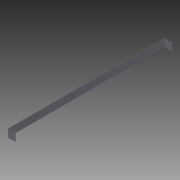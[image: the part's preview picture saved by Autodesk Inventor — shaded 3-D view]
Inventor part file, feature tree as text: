
AUTODESK INVENTOR PART (.ipt)
format: ipt  version: 2013 (Build 170138000, 138)  size: 81,920 bytes
history: native  units: in
note: dims shown in document units (in); Inventor stores cm internally (conversion verified against a paired STEP export)
features: extrude x2, sketch x2
ambient origin geometry x8: Origin, YZ Plane, XZ Plane, XY Plane, X Axis, Y Axis, Z Axis, Center Point
bodies: Solid1 (feature_tree)
feature tree (4):
  extrude  "Extrusion1"  Depth=20.5in
  extrude  "Extrusion2"  Depth=0.01in
  sketch  "Sketch1"  dims[d0=1.0in d1=20.5in]
  sketch  "Sketch2"  dims[d2=0.01in d3=0.0in d4=0.01in d5=1.0in d6=0.01in d7=1.0in d8=1.0in d9=0.0in]
